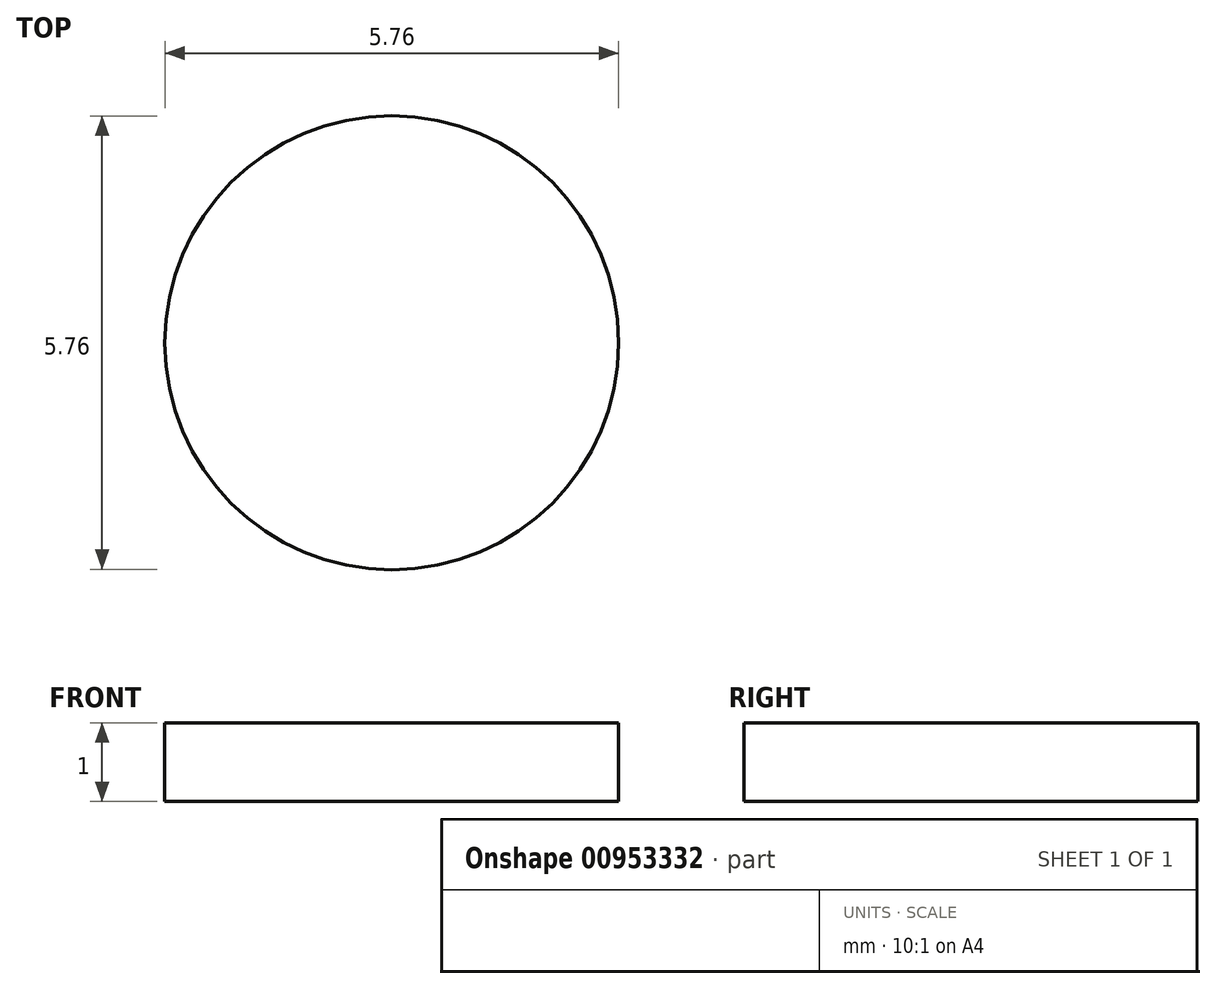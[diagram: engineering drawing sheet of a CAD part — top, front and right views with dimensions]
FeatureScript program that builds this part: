
annotation { "Feature Type Name" : "Feature", "Feature Type Description" : "" }
export const myFeature = defineFeature(function(context is Context, id is Id, definition is map)
    precondition{}
    {
        {
            var Q0;
            Q0=qCreatedBy(makeId("Top.planeOp"),FACE);
            var sketch = newSketch(context, id + "F0", { "sketchPlane" : qUnion([Q0])});
            skLineSegment(sketch, "E0.bottom", {"start": v(-10.52, 18.3) * mm, "end": v(10.52, 18.3) * mm});
            skLineSegment(sketch, "E0.top", {"start": v(-10.52, -25.7) * mm, "end": v(10.52, -25.7) * mm});
            skLineSegment(sketch, "E0.left", {"start": v(-10.52, 18.3) * mm, "end": v(-10.52, -25.7) * mm});
            skLineSegment(sketch, "E0.right", {"start": v(10.52, 18.3) * mm, "end": v(10.52, -25.7) * mm});
            skPoint(sketch, "E0.middle", {"position": v(0, -3.7) * mm});
            skLineSegment(sketch, "E1.bottom", {"start": v(-14.12, 24.36) * mm, "end": v(13.94, 24.36) * mm});
            skLineSegment(sketch, "E1.top", {"start": v(-14.12, -29.1) * mm, "end": v(13.94, -29.1) * mm});
            skLineSegment(sketch, "E1.left", {"start": v(-14.12, 24.36) * mm, "end": v(-14.12, -29.1) * mm});
            skLineSegment(sketch, "E1.right", {"start": v(13.94, 24.36) * mm, "end": v(13.94, -29.1) * mm});
            skCircle(sketch, "E2", {"center": v(-7.68, 21.7) * mm, "radius": 1.58 * mm});
            skLineSegment(sketch, "E3", {"start": v(-2, 21.33) * mm, "end": v(4.83, 21.33) * mm});
            skLineSegment(sketch, "E4.top", {"start": v(-2, 19.81) * mm, "end": v(4.83, 19.81) * mm});
            skLineSegment(sketch, "E4.left", {"start": v(-2, 21.33) * mm, "end": v(-2, 19.81) * mm});
            skLineSegment(sketch, "E4.right", {"start": v(4.83, 21.33) * mm, "end": v(4.83, 19.81) * mm});
            skCircle(sketch, "E5", {"center": v(0, -20.38) * mm, "radius": 2.88 * mm});
            skSolve(sketch);
        }
        {
            var Q0;
            Q0=makeQuery(id+"F0.imprint","IMPRINT",FACE,{"disambiguationData":[TD([[makeQuery(id+"F0.imprint","IMPRINT",EDGE,{"derivedFrom":sQuery(id+"F0.wireOp",EDGE,"E5")}),1.0]])]});
            extrude(context, id + "F1", {"entities" : qUnion([Q0]), "depth" : 1 * mm, "offsetDistance" : 25.4 * mm});
        }
    });
